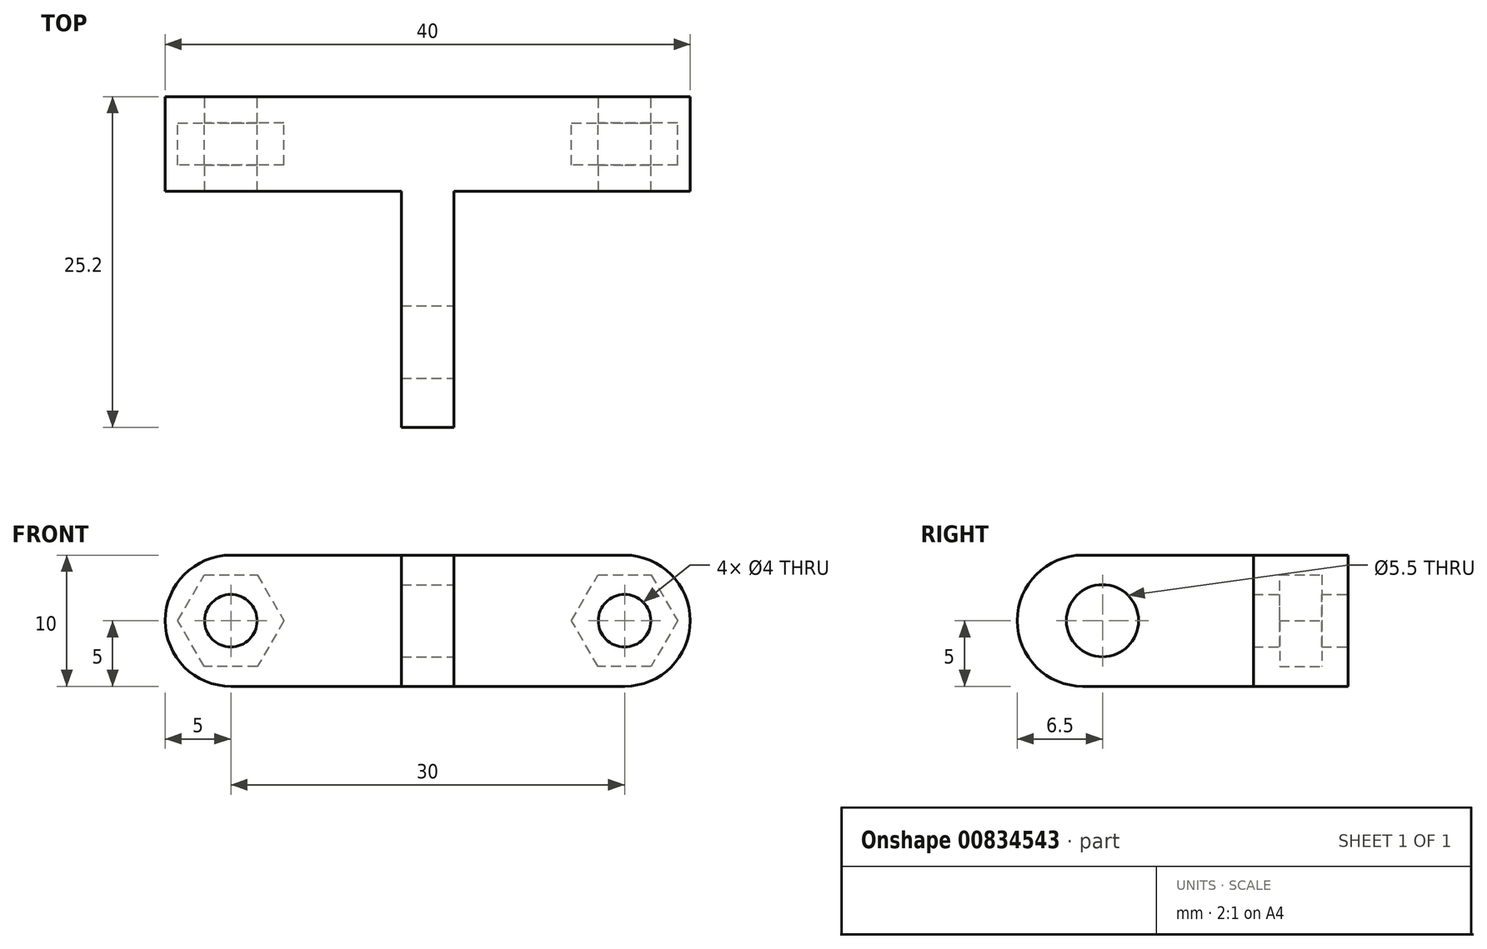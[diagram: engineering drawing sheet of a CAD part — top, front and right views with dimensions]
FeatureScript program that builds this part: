
annotation { "Feature Type Name" : "Feature", "Feature Type Description" : "" }
export const myFeature = defineFeature(function(context is Context, id is Id, definition is map)
    precondition{}
    {
        {
            var Q0;
            Q0=qCreatedBy(makeId("Front.planeOp"),FACE);
            var sketch = newSketch(context, id + "F0", { "sketchPlane" : qUnion([Q0])});
            skLineSegment(sketch, "E0.bottom", {"start": v(20, -5) * mm, "end": v(-20, -5) * mm});
            skLineSegment(sketch, "E0.top", {"start": v(20, 5) * mm, "end": v(-20, 5) * mm});
            skLineSegment(sketch, "E0.left", {"start": v(20, -5) * mm, "end": v(20, 5) * mm});
            skLineSegment(sketch, "E0.right", {"start": v(-20, -5) * mm, "end": v(-20, 5) * mm});
            skPoint(sketch, "E0.middle", {"position": v(0, 0) * mm});
            skCircle(sketch, "E1", {"center": v(-15, 0) * mm, "radius": 2 * mm});
            skCircle(sketch, "E2", {"center": v(15, 0) * mm, "radius": 2 * mm});
            skSolve(sketch);
        }
        {
            var Q0;
            Q0=makeQuery(id+"F0.imprint","IMPRINT",FACE,{"disambiguationData":[TD([[makeQuery(id+"F0.imprint","IMPRINT",EDGE,{"derivedFrom":sQuery(id+"F0.wireOp",EDGE,"E0.bottom")}),-1.0]])]});
            extrude(context, id + "F1", {"entities" : qUnion([Q0]), "depth" : 2 * mm, "offsetDistance" : 25 * mm});
        }
        {
            var Q0;
            Q0=makeQuery(id+"F1.opExtrude","CAP_FACE",FACE,{"disambiguationData":[OSD([sQuery(id+"F0.wireOp",EDGE,"E0.bottom"),sQuery(id+"F0.wireOp",EDGE,"E0.top"),sQuery(id+"F0.wireOp",EDGE,"E0.left"),sQuery(id+"F0.wireOp",EDGE,"E0.right"),sQuery(id+"F0.wireOp",EDGE,"E1"),sQuery(id+"F0.wireOp",EDGE,"E2")])],"isStart":false});
            var sketch = newSketch(context, id + "F2", { "sketchPlane" : qUnion([Q0])});
            skCircle(sketch, "E3.cCircle", {"center": v(-15, 0) * mm, "radius": 3.5 * mm, "construction": true});
            skLineSegment(sketch, "E3.0", {"start": v(-12.98, -3.5) * mm, "end": v(-17.02, -3.5) * mm});
            skLineSegment(sketch, "E3.1", {"start": v(-17.02, -3.5) * mm, "end": v(-19.04, 0) * mm});
            skLineSegment(sketch, "E3.2", {"start": v(-19.04, 0) * mm, "end": v(-17.02, 3.5) * mm});
            skLineSegment(sketch, "E3.3", {"start": v(-17.02, 3.5) * mm, "end": v(-12.98, 3.5) * mm});
            skLineSegment(sketch, "E3.4", {"start": v(-12.98, 3.5) * mm, "end": v(-10.96, 0) * mm});
            skLineSegment(sketch, "E3.5", {"start": v(-10.96, 0) * mm, "end": v(-12.98, -3.5) * mm});
            skPoint(sketch, "E3.0.midPoint", {"position": v(-15, -3.5) * mm});
            skCircle(sketch, "E4.cCircle", {"center": v(15, 0) * mm, "radius": 3.5 * mm, "construction": true});
            skLineSegment(sketch, "E4.0", {"start": v(17.02, -3.5) * mm, "end": v(12.98, -3.5) * mm});
            skLineSegment(sketch, "E4.1", {"start": v(12.98, -3.5) * mm, "end": v(10.96, 0) * mm});
            skLineSegment(sketch, "E4.2", {"start": v(10.96, 0) * mm, "end": v(12.98, 3.5) * mm});
            skLineSegment(sketch, "E4.3", {"start": v(12.98, 3.5) * mm, "end": v(17.02, 3.5) * mm});
            skLineSegment(sketch, "E4.4", {"start": v(17.02, 3.5) * mm, "end": v(19.04, 0) * mm});
            skLineSegment(sketch, "E4.5", {"start": v(19.04, 0) * mm, "end": v(17.02, -3.5) * mm});
            skPoint(sketch, "E4.0.midPoint", {"position": v(15, -3.5) * mm});
            skSolve(sketch);
        }
        {
            var Q0;
            Q0=makeQuery(id+"F2.imprint","IMPRINT",FACE,{"disambiguationData":[TD([[makeQuery(id+"F2.imprint","IMPRINT",EDGE,{"derivedFrom":sQuery(id+"F2.wireOp",EDGE,"E3.0")}),1.0]])]});
            extrude(context, id + "F3", {"entities" : qUnion([Q0]), "operationType" : NewBodyOperationType.ADD, "depth" : 3.2 * mm, "offsetDistance" : 25 * mm});
        }
        {
            var Q0;
            Q0 = qSketchRegion(id + "F0", true);
            extrude(context, id + "F4", {"entities" : qUnion([Q0]), "operationType" : NewBodyOperationType.ADD, "depth" : 7.2 * mm, "offsetDistance" : 25 * mm, "hasSecondDirection" : true, "secondDirectionOppositeDirection" : false, "secondDirectionDepth" : 5.2 * mm});
        }
        {
            var Q0;
            Q0=makeQuery(id+"F4.opExtrude","CAP_FACE",FACE,{"disambiguationData":[OSD([sQuery(id+"F0.wireOp",EDGE,"E0.bottom"),sQuery(id+"F0.wireOp",EDGE,"E0.top"),sQuery(id+"F0.wireOp",EDGE,"E0.left"),sQuery(id+"F0.wireOp",EDGE,"E0.right"),sQuery(id+"F0.wireOp",EDGE,"E1"),sQuery(id+"F0.wireOp",EDGE,"E2")])],"isStart":false});
            var sketch = newSketch(context, id + "F5", { "sketchPlane" : qUnion([Q0])});
            skPoint(sketch, "E5.0", {"position": v(0, 0) * mm});
            skLineSegment(sketch, "E6.bottom", {"start": v(2, -5) * mm, "end": v(-2, -5) * mm});
            skLineSegment(sketch, "E6.top", {"start": v(2, 5) * mm, "end": v(-2, 5) * mm});
            skLineSegment(sketch, "E6.left", {"start": v(2, -5) * mm, "end": v(2, 5) * mm});
            skLineSegment(sketch, "E6.right", {"start": v(-2, -5) * mm, "end": v(-2, 5) * mm});
            skSolve(sketch);
        }
        {
            var Q0;
            Q0 = qSketchRegion(id + "F5", true);
            extrude(context, id + "F6", {"entities" : qUnion([Q0]), "operationType" : NewBodyOperationType.ADD, "depth" : 18 * mm, "offsetDistance" : 25 * mm});
        }
        {
            var Q0;
            Q0=makeQuery(id+"F6.opExtrude","SWEPT_FACE",FACE,{"disambiguationData":[OSD([sQuery(id+"F5.wireOp",EDGE,"E6.left")])]});
            var sketch = newSketch(context, id + "F7", { "sketchPlane" : qUnion([Q0])});
            skCircle(sketch, "E7", {"center": v(-18.7, 0) * mm, "radius": 2.75 * mm});
            skPoint(sketch, "E7.centerSnap0", {"position": v(-25.2, 0) * mm});
            skSolve(sketch);
        }
        {
            var Q0;
            Q0 = qSketchRegion(id + "F7", true);
            extrude(context, id + "F8", {"entities" : qUnion([Q0]), "operationType" : NewBodyOperationType.REMOVE, "oppositeDirection" : true, "depth" : 25 * mm, "offsetDistance" : 25 * mm});
        }
        {
            var Q0;
            Q0=makeQuery(id+"F6.opExtrude","CAP_EDGE",EDGE,{"disambiguationData":[OSD([sQuery(id+"F5.wireOp",EDGE,"E6.top")])],"isStart":false});
            var Q1;
            Q1=makeQuery(id+"F6.opExtrude","CAP_EDGE",EDGE,{"disambiguationData":[OSD([sQuery(id+"F5.wireOp",EDGE,"E6.bottom")])],"isStart":false});
            var Q2;
            {var subQ0=sQuery(id+"F0.wireOp",EDGE,"E0.left");var subQ1=sQuery(id+"F0.wireOp",EDGE,"E0.top");Q2=makeQuery(id+"F4.boolean.opBoolean","MERGE",EDGE,{"derivedFrom":[makeQuery(id+"F3.boolean.opBoolean","MERGE",EDGE,{"derivedFrom":[makeQuery(id+"F1.opExtrude","SWEPT_EDGE",EDGE,{"disambiguationData":[OSD([subQ1,subQ0])]}),makeQuery(id+"F3.opExtrude","SWEPT_EDGE",EDGE,{"disambiguationData":[OSD([subQ1,subQ0])]})]}),makeQuery(id+"F4.opExtrude","SWEPT_EDGE",EDGE,{"disambiguationData":[OSD([subQ1,subQ0])]})]});}
            var Q3;
            {var subQ0=sQuery(id+"F0.wireOp",EDGE,"E0.left");var subQ1=sQuery(id+"F0.wireOp",EDGE,"E0.bottom");Q3=makeQuery(id+"F4.boolean.opBoolean","MERGE",EDGE,{"derivedFrom":[makeQuery(id+"F3.boolean.opBoolean","MERGE",EDGE,{"derivedFrom":[makeQuery(id+"F1.opExtrude","SWEPT_EDGE",EDGE,{"disambiguationData":[OSD([subQ1,subQ0])]}),makeQuery(id+"F3.opExtrude","SWEPT_EDGE",EDGE,{"disambiguationData":[OSD([subQ1,subQ0])]})]}),makeQuery(id+"F4.opExtrude","SWEPT_EDGE",EDGE,{"disambiguationData":[OSD([subQ1,subQ0])]})]});}
            var Q4;
            {var subQ0=sQuery(id+"F0.wireOp",EDGE,"E0.right");var subQ1=sQuery(id+"F0.wireOp",EDGE,"E0.top");Q4=makeQuery(id+"F4.boolean.opBoolean","MERGE",EDGE,{"derivedFrom":[makeQuery(id+"F3.boolean.opBoolean","MERGE",EDGE,{"derivedFrom":[makeQuery(id+"F1.opExtrude","SWEPT_EDGE",EDGE,{"disambiguationData":[OSD([subQ1,subQ0])]}),makeQuery(id+"F3.opExtrude","SWEPT_EDGE",EDGE,{"disambiguationData":[OSD([subQ1,subQ0])]})]}),makeQuery(id+"F4.opExtrude","SWEPT_EDGE",EDGE,{"disambiguationData":[OSD([subQ1,subQ0])]})]});}
            var Q5;
            {var subQ0=sQuery(id+"F0.wireOp",EDGE,"E0.right");var subQ1=sQuery(id+"F0.wireOp",EDGE,"E0.bottom");Q5=makeQuery(id+"F4.boolean.opBoolean","MERGE",EDGE,{"derivedFrom":[makeQuery(id+"F3.boolean.opBoolean","MERGE",EDGE,{"derivedFrom":[makeQuery(id+"F1.opExtrude","SWEPT_EDGE",EDGE,{"disambiguationData":[OSD([subQ1,subQ0])]}),makeQuery(id+"F3.opExtrude","SWEPT_EDGE",EDGE,{"disambiguationData":[OSD([subQ1,subQ0])]})]}),makeQuery(id+"F4.opExtrude","SWEPT_EDGE",EDGE,{"disambiguationData":[OSD([subQ1,subQ0])]})]});}
            fillet(context, id + "F9", {"entities" : qUnion([Q0, Q1, Q2, Q3, Q4, Q5]), "radius" : 5 * mm, "tangentPropagation" : true, "allowEdgeOverflow" : false});
        }
    });
